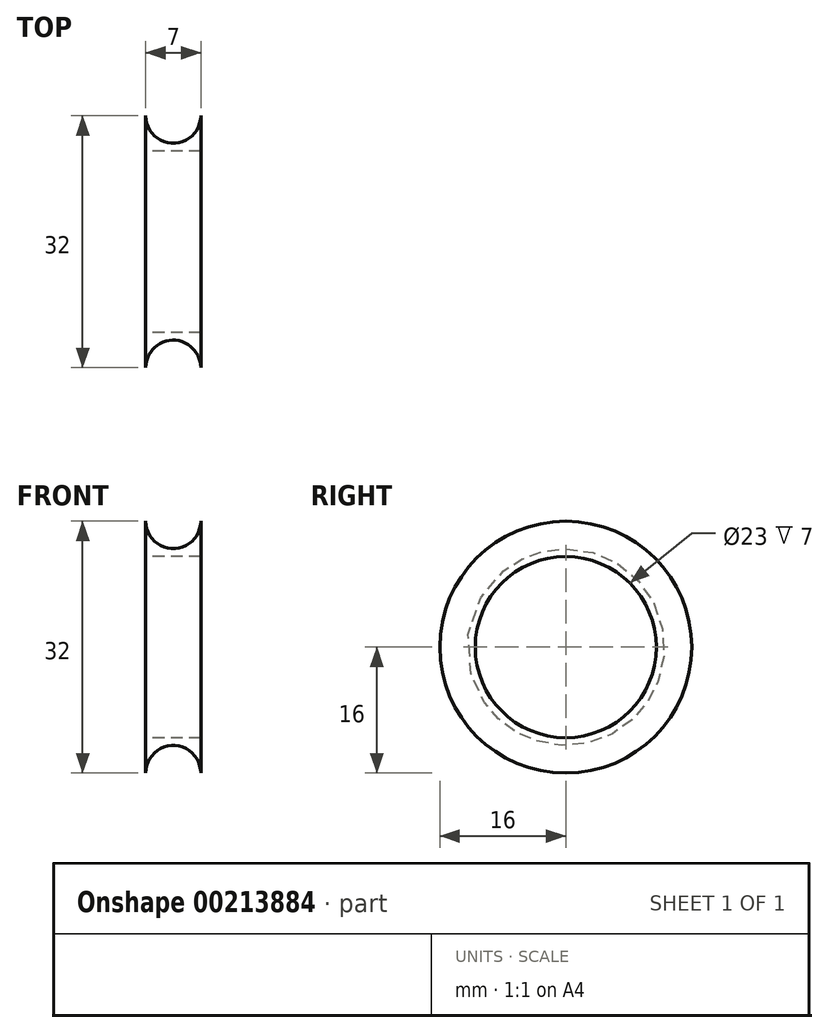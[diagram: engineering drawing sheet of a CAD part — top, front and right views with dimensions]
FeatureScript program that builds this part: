
annotation { "Feature Type Name" : "Feature", "Feature Type Description" : "" }
export const myFeature = defineFeature(function(context is Context, id is Id, definition is map)
    precondition{}
    {
        {
            var Q0;
            Q0=qCreatedBy(makeId("Top.planeOp"),FACE);
            var sketch = newSketch(context, id + "F0", { "sketchPlane" : qUnion([Q0])});
            skPoint(sketch, "E0", {"position": v(0, 11) * mm});
            skLineSegment(sketch, "E1", {"start": v(0, 11) * mm, "end": v(0, 16) * mm});
            skLineSegment(sketch, "E2", {"start": v(7, 16) * mm, "end": v(7, 11) * mm});
            skLineSegment(sketch, "E3", {"start": v(7, 11) * mm, "end": v(0, 11) * mm});
            skArc(sketch, "E4", {"start": v(0, 16) * mm, "mid": v(3.5, 12.5) * mm, "end": v(7, 16) * mm});
            skLineSegment(sketch, "E5", {"start": v(0, 11) * mm, "end": v(0, 0) * mm});
            skLineSegment(sketch, "E6", {"start": v(0, 0) * mm, "end": v(7, 0) * mm});
            skLineSegment(sketch, "E7", {"start": v(7, 0) * mm, "end": v(7, 11) * mm});
            skSolve(sketch);
        }
        {
            var Q0;
            Q0=makeQuery(id+"F0.imprint","IMPRINT",FACE,{"disambiguationData":[TD([[makeQuery(id+"F0.imprint","IMPRINT",EDGE,{"derivedFrom":sQuery(id+"F0.wireOp",EDGE,"E3")}),1.0]])]});
            var Q1;
            Q1=makeQuery(id+"F0.imprint","IMPRINT",FACE,{"disambiguationData":[TD([[makeQuery(id+"F0.imprint","IMPRINT",EDGE,{"derivedFrom":sQuery(id+"F0.wireOp",EDGE,"E1")}),-1.0]])]});
            var Q2;
            Q2=sQuery(id+"F0.wireOp",EDGE,"E6");
            revolve(context, id + "F1", {"surfaceOperationType" : NewSurfaceOperationType.NEW, "entities" : qUnion([Q0, Q1]), "axis" : qUnion([Q2]), "revolveType" : RevolveType.FULL});
        }
        {
            var Q0;
            Q0=makeQuery(id+"F1.opRevolve","SWEPT_FACE",FACE,{"disambiguationData":[OSD([sQuery(id+"F0.wireOp",EDGE,"E1"),sQuery(id+"F0.wireOp",EDGE,"E5")])]});
            var sketch = newSketch(context, id + "F2", { "sketchPlane" : qUnion([Q0])});
            skCircle(sketch, "E8", {"center": v(0, 0) * mm, "radius": 22 * mm});
            skSolve(sketch);
        }
        {
            var Q0;
            Q0=makeQuery(id+"F2.imprint","IMPRINT",FACE,{"disambiguationData":[TD([[makeQuery(id+"F2.imprint","IMPRINT",EDGE,{"derivedFrom":sQuery(id+"F2.wireOp",EDGE,"E8")}),1.0]])]});
            extrude(context, id + "F3", {"entities" : qUnion([Q0]), "operationType" : NewBodyOperationType.REMOVE, "oppositeDirection" : true, "depth" : 25 * mm, "offsetDistance" : 25 * mm});
        }
        {
            var Q0;
            Q0=makeQuery(id+"F1.opRevolve","SWEPT_FACE",FACE,{"disambiguationData":[OSD([sQuery(id+"F0.wireOp",EDGE,"E1"),sQuery(id+"F0.wireOp",EDGE,"E5")])]});
            var sketch = newSketch(context, id + "F4", { "sketchPlane" : qUnion([Q0])});
            skCircle(sketch, "E9", {"center": v(0, 0) * mm, "radius": 11.5 * mm});
            skSolve(sketch);
        }
        {
            var Q0;
            Q0=makeQuery(id+"F4.imprint","IMPRINT",FACE,{"disambiguationData":[TD([[makeQuery(id+"F4.imprint","IMPRINT",EDGE,{"derivedFrom":sQuery(id+"F4.wireOp",EDGE,"E9")}),1.0]])]});
            extrude(context, id + "F5", {"entities" : qUnion([Q0]), "operationType" : NewBodyOperationType.REMOVE, "oppositeDirection" : true, "depth" : 25 * mm, "offsetDistance" : 25 * mm});
        }
    });
